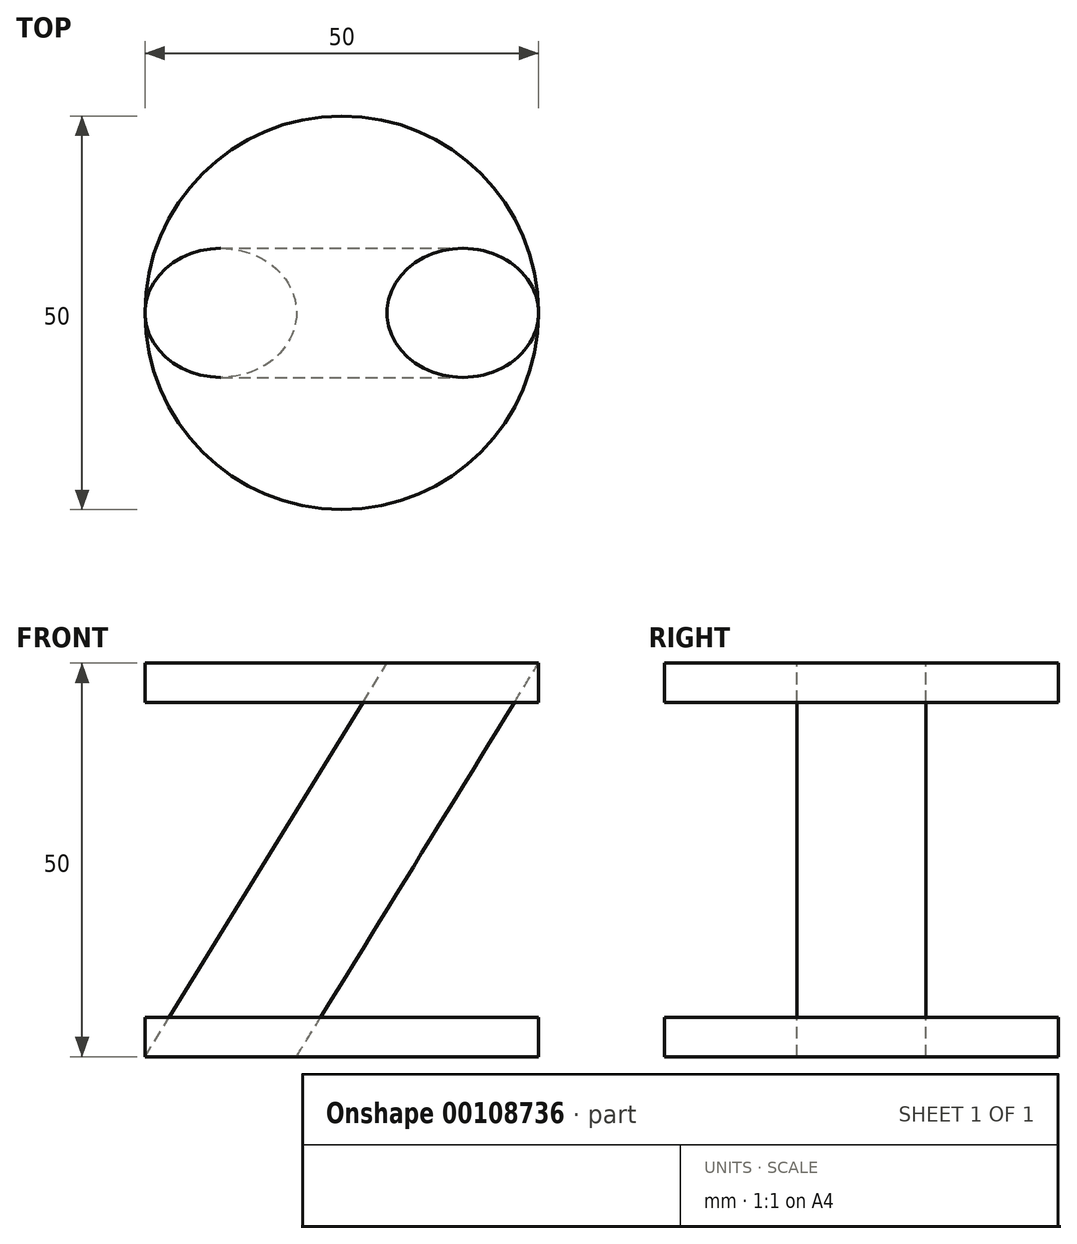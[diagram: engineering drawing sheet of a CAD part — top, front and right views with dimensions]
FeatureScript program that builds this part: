
annotation { "Feature Type Name" : "Feature", "Feature Type Description" : "" }
export const myFeature = defineFeature(function(context is Context, id is Id, definition is map)
    precondition{}
    {
        {
            var Q0;
            Q0=qCreatedBy(makeId("Front.planeOp"),FACE);
            var sketch = newSketch(context, id + "F0", { "sketchPlane" : qUnion([Q0])});
            skLineSegment(sketch, "E0.bottom", {"start": v(25, 20) * mm, "end": v(-25, 20) * mm});
            skLineSegment(sketch, "E0.top", {"start": v(25, 25) * mm, "end": v(-25, 25) * mm});
            skLineSegment(sketch, "E0.left", {"start": v(25, 20) * mm, "end": v(25, 25) * mm});
            skLineSegment(sketch, "E0.right", {"start": v(-25, 20) * mm, "end": v(-25, 25) * mm});
            skPoint(sketch, "E0.middle", {"position": v(0, 22.5) * mm});
            skLineSegment(sketch, "E1.bottom", {"start": v(25, -25) * mm, "end": v(-25, -25) * mm});
            skLineSegment(sketch, "E1.top", {"start": v(25, -20) * mm, "end": v(-25, -20) * mm});
            skLineSegment(sketch, "E1.left", {"start": v(25, -25) * mm, "end": v(25, -20) * mm});
            skLineSegment(sketch, "E1.right", {"start": v(-25, -25) * mm, "end": v(-25, -20) * mm});
            skPoint(sketch, "E1.middle", {"position": v(0, -22.5) * mm});
            skLineSegment(sketch, "E2", {"start": v(0, 22.5) * mm, "end": v(0, -22.5) * mm, "construction": true});
            skLineSegment(sketch, "E3", {"start": v(35.85, 42.65) * mm, "end": v(-21.35, -50.35) * mm});
            skPoint(sketch, "E4", {"position": v(0, -20) * mm});
            skLineSegment(sketch, "E5", {"start": v(-28.33, -46.06) * mm, "end": v(-21.35, -50.35) * mm});
            skLineSegment(sketch, "E6", {"start": v(28.87, 46.94) * mm, "end": v(35.85, 42.65) * mm});
            skLineSegment(sketch, "E7", {"start": v(28.87, 46.94) * mm, "end": v(-28.33, -46.06) * mm});
            skLineSegment(sketch, "E8", {"start": v(0, 25) * mm, "end": v(0, -25) * mm});
            skSolve(sketch);
        }
        {
            var Q0;
            {var subQ0=sQuery(id+"F0.wireOp",EDGE,"E3");var subQ1=sQuery(id+"F0.wireOp",EDGE,"E0.bottom");var subQ2=makeQuery(id+"F0.imprint","INTERSECT",VERTEX,{"derivedFrom":[subQ1,subQ0]});Q0=makeQuery(id+"F0.imprint","IMPRINT",FACE,{"disambiguationData":[TD([[makeQuery(id+"F0.imprint","IMPRINT",EDGE,{"disambiguationData":[TD([[subQ2,-1.0]])],"derivedFrom":subQ1}),1.0]])]});}
            var Q1;
            {var subQ0=sQuery(id+"F0.wireOp",EDGE,"E3");var subQ1=sQuery(id+"F0.wireOp",EDGE,"E0.bottom");var subQ2=makeQuery(id+"F0.imprint","INTERSECT",VERTEX,{"derivedFrom":[subQ1,subQ0]});Q1=makeQuery(id+"F0.imprint","IMPRINT",FACE,{"disambiguationData":[TD([[makeQuery(id+"F0.imprint","IMPRINT",EDGE,{"disambiguationData":[TD([[subQ2,-1.0]])],"derivedFrom":subQ1}),-1.0]])]});}
            var Q2;
            {var subQ5=sQuery(id+"F0.wireOp",EDGE,"E6");Q2=makeQuery(id+"F0.imprint","IMPRINT",FACE,{"disambiguationData":[TD([[makeQuery(id+"F0.imprint","IMPRINT",EDGE,{"derivedFrom":subQ5}),-1.0]])]});}
            var Q3;
            {var subQ0=sQuery(id+"F0.wireOp",EDGE,"E3");var subQ1=sQuery(id+"F0.wireOp",EDGE,"E1.bottom");var subQ2=makeQuery(id+"F0.imprint","INTERSECT",VERTEX,{"derivedFrom":[subQ1,subQ0]});Q3=makeQuery(id+"F0.imprint","IMPRINT",FACE,{"disambiguationData":[TD([[makeQuery(id+"F0.imprint","IMPRINT",EDGE,{"disambiguationData":[TD([[subQ2,-1.0]])],"derivedFrom":subQ1}),-1.0]])]});}
            var Q4;
            {var subQ5=sQuery(id+"F0.wireOp",EDGE,"E5");Q4=makeQuery(id+"F0.imprint","IMPRINT",FACE,{"disambiguationData":[TD([[makeQuery(id+"F0.imprint","IMPRINT",EDGE,{"derivedFrom":subQ5}),1.0]])]});}
            var Q5;
            {var subQ0=sQuery(id+"F0.wireOp",EDGE,"E7");var subQ1=sQuery(id+"F0.wireOp",EDGE,"E1.top");var subQ2=makeQuery(id+"F0.imprint","INTERSECT",VERTEX,{"derivedFrom":[subQ1,subQ0]});Q5=makeQuery(id+"F0.imprint","IMPRINT",FACE,{"disambiguationData":[TD([[makeQuery(id+"F0.imprint","IMPRINT",EDGE,{"disambiguationData":[TD([[subQ2,1.0]])],"derivedFrom":subQ1}),-1.0]])]});}
            var Q6;
            Q6=sQuery(id+"F0.wireOp",EDGE,"E7");
            revolve(context, id + "F1", {"entities" : qUnion([Q0, Q1, Q2, Q3, Q4, Q5]), "axis" : qUnion([Q6]), "revolveType" : RevolveType.FULL});
        }
        {
            var Q0;
            {var subQ0=sQuery(id+"F0.wireOp",EDGE,"E0.right");Q0=makeQuery(id+"F0.imprint","IMPRINT",FACE,{"disambiguationData":[TD([[makeQuery(id+"F0.imprint","IMPRINT",EDGE,{"derivedFrom":subQ0}),-1.0]])]});}
            var Q1;
            {var subQ0=sQuery(id+"F0.wireOp",EDGE,"E8");var subQ1=sQuery(id+"F0.wireOp",EDGE,"E1.bottom");var subQ2=makeQuery(id+"F0.imprint","INTERSECT",VERTEX,{"derivedFrom":[subQ1,subQ0]});Q1=makeQuery(id+"F0.imprint","IMPRINT",FACE,{"disambiguationData":[TD([[makeQuery(id+"F0.imprint","IMPRINT",EDGE,{"disambiguationData":[TD([[subQ2,-1.0]])],"derivedFrom":subQ1}),-1.0]])]});}
            var Q2;
            {var subQ0=sQuery(id+"F0.wireOp",EDGE,"E3");var subQ1=sQuery(id+"F0.wireOp",EDGE,"E1.bottom");var subQ2=makeQuery(id+"F0.imprint","INTERSECT",VERTEX,{"derivedFrom":[subQ1,subQ0]});Q2=makeQuery(id+"F0.imprint","IMPRINT",FACE,{"disambiguationData":[TD([[makeQuery(id+"F0.imprint","IMPRINT",EDGE,{"disambiguationData":[TD([[subQ2,-1.0]])],"derivedFrom":subQ1}),-1.0]])]});}
            var Q3;
            {var subQ0=sQuery(id+"F0.wireOp",EDGE,"E1.right");Q3=makeQuery(id+"F0.imprint","IMPRINT",FACE,{"disambiguationData":[TD([[makeQuery(id+"F0.imprint","IMPRINT",EDGE,{"derivedFrom":subQ0}),-1.0]])]});}
            var Q4;
            Q4=sQuery(id+"F0.wireOp",EDGE,"E8");
            revolve(context, id + "F2", {"entities" : qUnion([Q0, Q1, Q2, Q3]), "axis" : qUnion([Q4]), "revolveType" : RevolveType.FULL});
        }
        {
            var Q0;
            Q0=makeQuery(id+"F2.opRevolve","SWEPT_FACE",FACE,{"disambiguationData":[OSD([sQuery(id+"F0.wireOp",EDGE,"E0.top")])]});
            var sketch = newSketch(context, id + "F3", { "sketchPlane" : qUnion([Q0])});
            skCircle(sketch, "E9.0", {"center": v(0, 0) * mm, "radius": 25 * mm});
            skCircle(sketch, "E10", {"center": v(0, 0) * mm, "radius": 65.55 * mm});
            skSolve(sketch);
        }
        {
            var Q0;
            Q0=makeQuery(id+"F3.imprint","IMPRINT",FACE,{"disambiguationData":[TD([[makeQuery(id+"F3.imprint","IMPRINT",EDGE,{"derivedFrom":sQuery(id+"F3.wireOp",EDGE,"E9.0")}),-1.0]])]});
            var Q1;
            Q1=makeQuery(id+"F3.imprint","IMPRINT",FACE,{"disambiguationData":[TD([[makeQuery(id+"F3.imprint","IMPRINT",EDGE,{"derivedFrom":sQuery(id+"F3.wireOp",EDGE,"E9.0")}),1.0]])]});
            extrude(context, id + "F4", {"entities" : qUnion([Q0, Q1]), "operationType" : NewBodyOperationType.REMOVE, "depth" : 36.52 * mm});
        }
        {
            var Q0;
            Q0=makeQuery(id+"F2.opRevolve","SWEPT_FACE",FACE,{"disambiguationData":[OSD([sQuery(id+"F0.wireOp",EDGE,"E1.bottom")])]});
            var sketch = newSketch(context, id + "F5", { "sketchPlane" : qUnion([Q0])});
            skCircle(sketch, "E11", {"center": v(0, 0) * mm, "radius": 55.27 * mm});
            skSolve(sketch);
        }
        {
            var Q0;
            Q0 = qSketchRegion(id + "F5", true);
            extrude(context, id + "F6", {"entities" : qUnion([Q0]), "operationType" : NewBodyOperationType.REMOVE, "depth" : 53.37 * mm});
        }
    });
